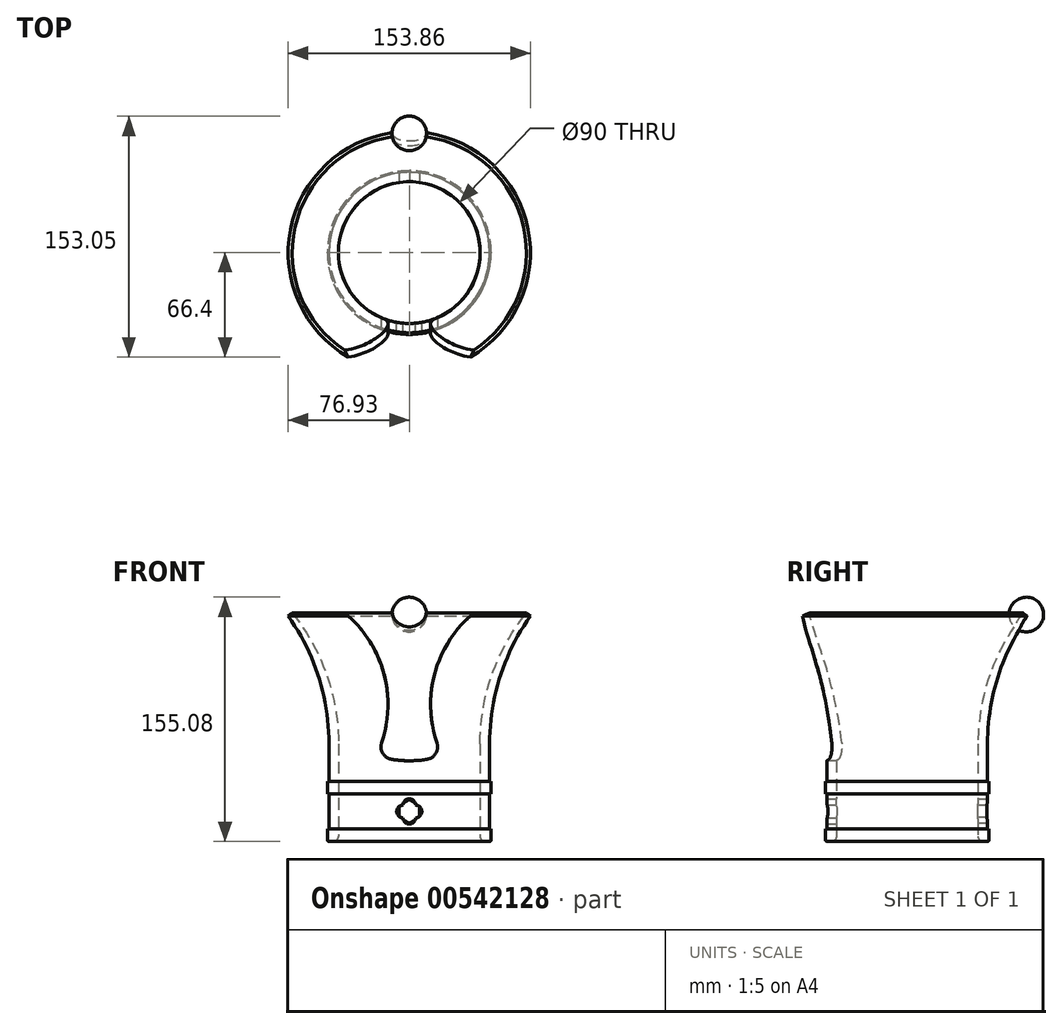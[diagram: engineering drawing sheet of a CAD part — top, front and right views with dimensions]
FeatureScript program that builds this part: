
annotation { "Feature Type Name" : "Feature", "Feature Type Description" : "" }
export const myFeature = defineFeature(function(context is Context, id is Id, definition is map)
    precondition{}
    {
        {
            var Q0;
            Q0=qCreatedBy(makeId("Front.planeOp"),FACE);
            var sketch = newSketch(context, id + "F0", { "sketchPlane" : qUnion([Q0])});
            skLineSegment(sketch, "E0", {"start": v(0, 0) * mm, "end": v(0, 134.17) * mm});
            skLineSegment(sketch, "E1", {"start": v(-45, 0) * mm, "end": v(-52, 0) * mm});
            skLineSegment(sketch, "E2", {"start": v(-45, 0) * mm, "end": v(-45, 62) * mm});
            skArc(sketch, "E3", {"start": v(-45, 62) * mm, "mid": v(-52.56, 106.02) * mm, "end": v(-74.36, 145) * mm});
            skLineSegment(sketch, "E4", {"start": v(-52, 0) * mm, "end": v(-52, 8) * mm});
            skLineSegment(sketch, "E5", {"start": v(-52, 8) * mm, "end": v(-51, 8) * mm});
            skLineSegment(sketch, "E6", {"start": v(-51, 8) * mm, "end": v(-51, 30) * mm});
            skLineSegment(sketch, "E7", {"start": v(-51, 30) * mm, "end": v(-52, 30) * mm});
            skLineSegment(sketch, "E8", {"start": v(-52, 30) * mm, "end": v(-52, 38) * mm});
            skLineSegment(sketch, "E9", {"start": v(-52, 38) * mm, "end": v(-51, 38) * mm});
            skLineSegment(sketch, "E10", {"start": v(-51, 38) * mm, "end": v(-51, 62) * mm});
            skArc(sketch, "E11", {"start": v(-51, 62) * mm, "mid": v(-57.64, 104.6) * mm, "end": v(-76.93, 143.17) * mm});
            skLineSegment(sketch, "E12", {"start": v(-191, 62) * mm, "end": v(-74.36, 145) * mm});
            skSolve(sketch);
        }
        {
            var Q0;
            Q0=makeQuery(id+"F0.imprint","IMPRINT",FACE,{"disambiguationData":[TD([[makeQuery(id+"F0.imprint","IMPRINT",EDGE,{"derivedFrom":sQuery(id+"F0.wireOp",EDGE,"E1")}),-1.0]])]});
            var Q1;
            Q1=sQuery(id+"F0.wireOp",EDGE,"E0");
            revolve(context, id + "F1", {"entities" : qUnion([Q0]), "axis" : qUnion([Q1]), "revolveType" : RevolveType.FULL});
        }
        {
            var Q0;
            Q0=qCreatedBy(makeId("Front.planeOp"),FACE);
            var sketch = newSketch(context, id + "F2", { "sketchPlane" : qUnion([Q0])});
            skArc(sketch, "E13", {"start": v(-11.32, 52.1) * mm, "mid": v(-5.68, 51.4) * mm, "end": v(0, 51.17) * mm});
            skLineSegment(sketch, "E14", {"start": v(0, 0) * mm, "end": v(0, 145) * mm});
            skArc(sketch, "E15", {"start": v(-17.57, 62.6) * mm, "mid": v(-16.36, 107.47) * mm, "end": v(-41, 145) * mm});
            skArc(sketch, "E16", {"start": v(-11.32, 52.1) * mm, "mid": v(-16.87, 55.9) * mm, "end": v(-17.57, 62.6) * mm});
            skLineSegment(sketch, "E17.0", {"start": v(41, 145) * mm, "end": v(-41, 145) * mm});
            skPoint(sketch, "E18.orphan", {"position": v(-74.36, 145) * mm});
            skArc(sketch, "E19.MirrorCS", {"start": v(17.57, 62.6) * mm, "mid": v(16.36, 107.47) * mm, "end": v(41, 145) * mm});
            skArc(sketch, "E20.MirrorCS", {"start": v(11.32, 52.1) * mm, "mid": v(16.87, 55.9) * mm, "end": v(17.57, 62.6) * mm});
            skArc(sketch, "E21.MirrorCS", {"start": v(11.32, 52.1) * mm, "mid": v(5.68, 51.4) * mm, "end": v(0, 51.17) * mm});
            skPoint(sketch, "E22.orphan", {"position": v(74.36, 145) * mm});
            skSolve(sketch);
        }
        {
            var Q0;
            Q0=qCreatedBy(makeId("Front.planeOp"),FACE);
            cPlane(context, id + "F3", {"entities" : qUnion([Q0]), "cplaneType" : CPlaneType.OFFSET, "offset" : 90 * mm, "width" : 150 * mm, "height" : 150 * mm});
        }
        {
            var Q0;
            Q0=qCreatedBy(id+"F3.planeOp",FACE);
            var sketch = newSketch(context, id + "F4", { "sketchPlane" : qUnion([Q0])});
            skArc(sketch, "E23.0", {"start": v(-17.57, 62.6) * mm, "mid": v(-16.36, 107.47) * mm, "end": v(-41, 145) * mm});
            skLineSegment(sketch, "E24.0", {"start": v(41, 145) * mm, "end": v(-41, 145) * mm});
            skArc(sketch, "E25.0", {"start": v(17.57, 62.6) * mm, "mid": v(16.36, 107.47) * mm, "end": v(41, 145) * mm});
            skArc(sketch, "E26.0", {"start": v(-11.32, 52.1) * mm, "mid": v(-16.87, 55.9) * mm, "end": v(-17.57, 62.6) * mm});
            skArc(sketch, "E27.0", {"start": v(-11.32, 52.1) * mm, "mid": v(-5.68, 51.4) * mm, "end": v(0, 51.17) * mm});
            skArc(sketch, "E28.0", {"start": v(11.32, 52.1) * mm, "mid": v(5.68, 51.4) * mm, "end": v(0, 51.17) * mm});
            skArc(sketch, "E29.0", {"start": v(11.32, 52.1) * mm, "mid": v(16.87, 55.9) * mm, "end": v(17.57, 62.6) * mm});
            skSolve(sketch);
        }
        {
            var Q0;
            Q0=makeQuery(id+"F4.imprint","IMPRINT",FACE,{"disambiguationData":[TD([[makeQuery(id+"F4.imprint","IMPRINT",EDGE,{"derivedFrom":sQuery(id+"F4.wireOp",EDGE,"E23.0")}),-1.0]])]});
            extrude(context, id + "F5", {"entities" : qUnion([Q0]), "operationType" : NewBodyOperationType.REMOVE, "oppositeDirection" : true, "depth" : 70 * mm, "offsetDistance" : 25 * mm});
        }
        {
            var Q0;
            Q0=qCreatedBy(makeId("Right.planeOp"),FACE);
            var sketch = newSketch(context, id + "F6", { "sketchPlane" : qUnion([Q0])});
            skPoint(sketch, "E30.0", {"position": v(76.93, 143.17) * mm});
            skPoint(sketch, "E31.0", {"position": v(74.36, 145) * mm});
            skLineSegment(sketch, "E32", {"start": v(76.93, 143.17) * mm, "end": v(74.36, 145) * mm});
            skArc(sketch, "E33", {"start": v(84.6, 137.7) * mm, "mid": v(82.02, 153.05) * mm, "end": v(66.68, 150.46) * mm});
            skLineSegment(sketch, "E34", {"start": v(74.36, 145) * mm, "end": v(84.6, 137.7) * mm});
            skLineSegment(sketch, "E35", {"start": v(74.36, 145) * mm, "end": v(66.68, 150.46) * mm});
            skSolve(sketch);
        }
        {
            var Q0;
            {var subQ0=sQuery(id+"F6.wireOp",EDGE,"E33");Q0=makeQuery(id+"F6.imprint","IMPRINT",FACE,{"disambiguationData":[TD([[makeQuery(id+"F6.imprint","IMPRINT",EDGE,{"derivedFrom":subQ0}),1.0]])]});}
            var Q1;
            Q1=sQuery(id+"F6.wireOp",EDGE,"E34");
            revolve(context, id + "F7", {"operationType" : NewBodyOperationType.ADD, "entities" : qUnion([Q0]), "axis" : qUnion([Q1]), "revolveType" : RevolveType.FULL});
        }
        {
            var Q0;
            Q0=makeQuery(id+"F1.opRevolve","SWEPT_EDGE",EDGE,{"disambiguationData":[OSD([sQuery(id+"F0.wireOp",EDGE,"E1"),sQuery(id+"F0.wireOp",EDGE,"E2")])]});
            fillet(context, id + "F8", {"entities" : qUnion([Q0]), "radius" : 3 * mm, "tangentPropagation" : true, "allowEdgeOverflow" : false});
        }
        {
            var Q0;
            Q0=makeQuery(id+"F1.opRevolve","SWEPT_EDGE",EDGE,{"disambiguationData":[OSD([sQuery(id+"F0.wireOp",EDGE,"E1"),sQuery(id+"F0.wireOp",EDGE,"E4")])]});
            fillet(context, id + "F9", {"entities" : qUnion([Q0]), "radius" : 1 * mm, "tangentPropagation" : true, "allowEdgeOverflow" : false});
        }
        {
            var Q0;
            Q0=qCreatedBy(makeId("Front.planeOp"),FACE);
            var sketch = newSketch(context, id + "F10", { "sketchPlane" : qUnion([Q0])});
            skLineSegment(sketch, "E36.0", {"start": v(52, 30) * mm, "end": v(-52, 30) * mm});
            skLineSegment(sketch, "E37.0", {"start": v(52, 8) * mm, "end": v(-52, 8) * mm});
            skLineSegment(sketch, "E38", {"start": v(0, 30) * mm, "end": v(0, 8) * mm});
            skCircle(sketch, "E39.cCircle", {"center": v(0, 19) * mm, "radius": 7.5 * mm, "construction": true});
            skLineSegment(sketch, "E39.0", {"start": v(0, 11.5) * mm, "end": v(-6.5, 15.25) * mm});
            skLineSegment(sketch, "E39.1", {"start": v(-6.5, 15.25) * mm, "end": v(-6.5, 22.75) * mm});
            skLineSegment(sketch, "E39.2", {"start": v(-6.5, 22.75) * mm, "end": v(0, 26.5) * mm});
            skLineSegment(sketch, "E39.3", {"start": v(0, 26.5) * mm, "end": v(6.5, 22.75) * mm});
            skLineSegment(sketch, "E39.4", {"start": v(6.5, 22.75) * mm, "end": v(6.5, 15.25) * mm});
            skLineSegment(sketch, "E39.5", {"start": v(6.5, 15.25) * mm, "end": v(0, 11.5) * mm});
            skSolve(sketch);
        }
        {
            var Q0;
            {var subQ0=sQuery(id+"F10.wireOp",EDGE,"E39.0");Q0=makeQuery(id+"F10.imprint","IMPRINT",FACE,{"disambiguationData":[TD([[makeQuery(id+"F10.imprint","IMPRINT",EDGE,{"derivedFrom":subQ0}),-1.0]])]});}
            var Q1;
            {var subQ2=sQuery(id+"F10.wireOp",EDGE,"E39.3");Q1=makeQuery(id+"F10.imprint","IMPRINT",FACE,{"disambiguationData":[TD([[makeQuery(id+"F10.imprint","IMPRINT",EDGE,{"derivedFrom":subQ2}),-1.0]])]});}
            extrude(context, id + "F11", {"entities" : qUnion([Q0, Q1]), "operationType" : NewBodyOperationType.REMOVE, "endBound" : BoundingType.THROUGH_ALL, "oppositeDirection" : true, "depth" : 25 * mm, "offsetDistance" : 25 * mm});
        }
        {
            var Q0;
            Q0=qCreatedBy(makeId("Front.planeOp"),FACE);
            var sketch = newSketch(context, id + "F12", { "sketchPlane" : qUnion([Q0])});
            skLineSegment(sketch, "E40.0", {"start": v(52, 8) * mm, "end": v(-52, 8) * mm});
            skLineSegment(sketch, "E41.0", {"start": v(52, 30) * mm, "end": v(-52, 30) * mm});
            skLineSegment(sketch, "E42", {"start": v(0, 30) * mm, "end": v(0, 8) * mm});
            skLineSegment(sketch, "E43", {"start": v(0, 19) * mm, "end": v(-11.78, 19) * mm});
            skCircle(sketch, "E44", {"center": v(0, 23) * mm, "radius": 4 * mm});
            skCircle(sketch, "E45", {"center": v(0, 15) * mm, "radius": 4 * mm});
            skCircle(sketch, "E46", {"center": v(-4, 19) * mm, "radius": 4 * mm});
            skLineSegment(sketch, "E47", {"start": v(0, 19) * mm, "end": v(9.64, 19) * mm});
            skCircle(sketch, "E48", {"center": v(4, 19) * mm, "radius": 4 * mm});
            skSolve(sketch);
        }
        {
            var Q0;
            Q0 = qSketchRegion(id + "F12", true);
            extrude(context, id + "F13", {"entities" : qUnion([Q0]), "operationType" : NewBodyOperationType.REMOVE, "endBound" : BoundingType.THROUGH_ALL, "depth" : 25 * mm, "offsetDistance" : 25 * mm});
        }
    });
